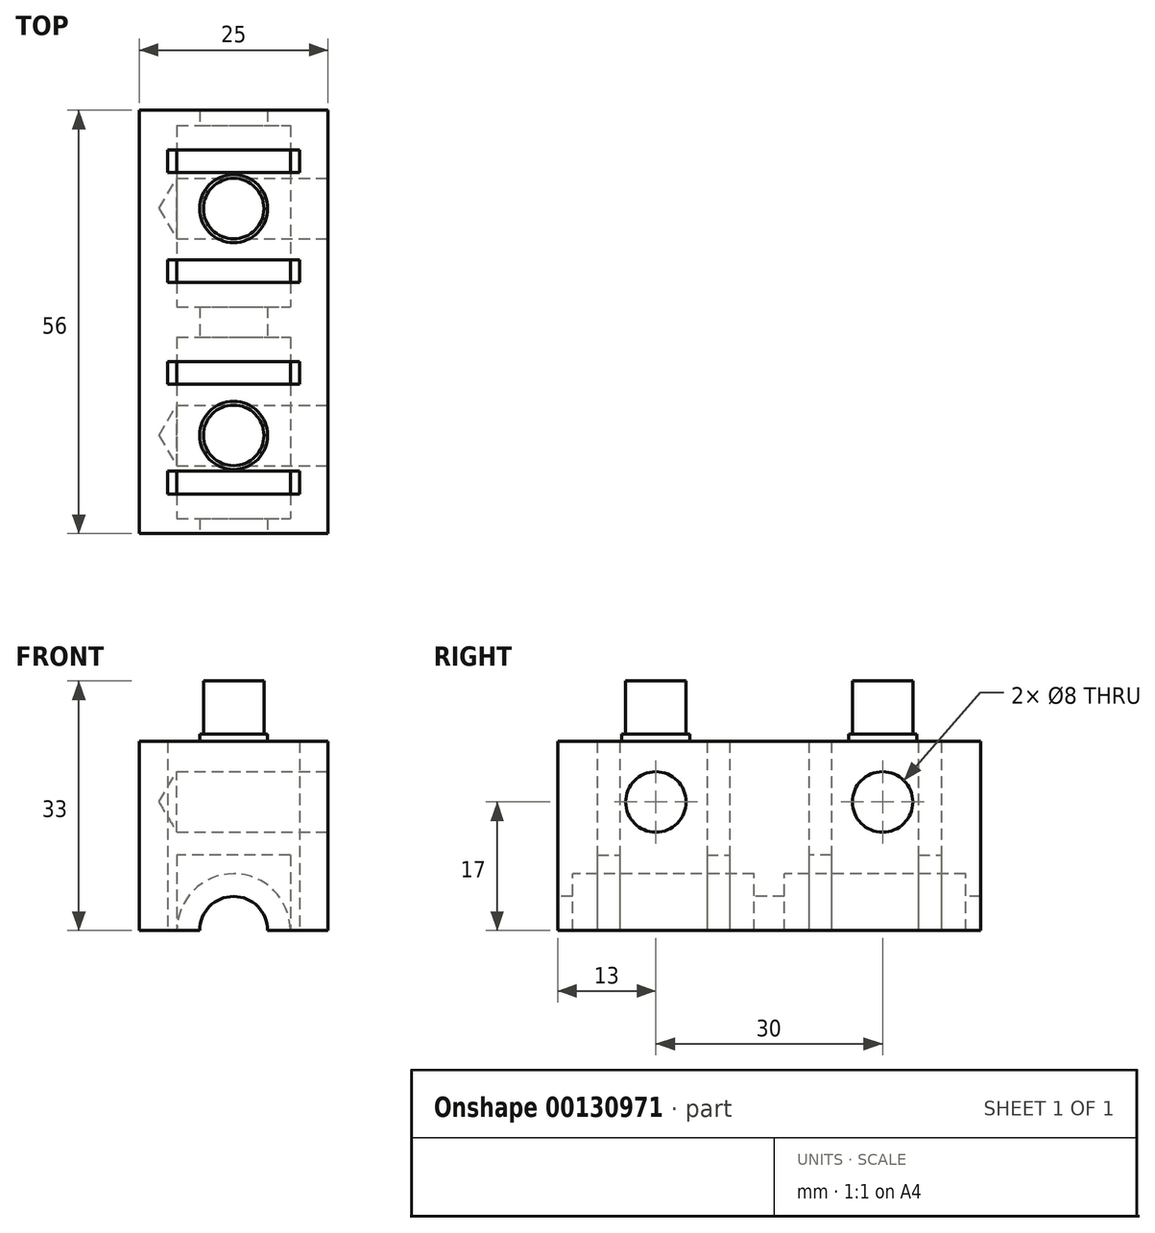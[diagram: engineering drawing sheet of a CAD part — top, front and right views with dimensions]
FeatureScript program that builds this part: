
annotation { "Feature Type Name" : "Feature", "Feature Type Description" : "" }
export const myFeature = defineFeature(function(context is Context, id is Id, definition is map)
    precondition{}
    {
        {
            var Q0;
            Q0=qCreatedBy(makeId("Top.planeOp"),FACE);
            var sketch = newSketch(context, id + "F0", { "sketchPlane" : qUnion([Q0])});
            skLineSegment(sketch, "E0.bottom", {"start": v(0, 0) * mm, "end": v(25, 0) * mm});
            skLineSegment(sketch, "E0.top", {"start": v(0, 56) * mm, "end": v(25, 56) * mm});
            skLineSegment(sketch, "E0.left", {"start": v(0, 0) * mm, "end": v(0, 56) * mm});
            skLineSegment(sketch, "E0.right", {"start": v(25, 0) * mm, "end": v(25, 56) * mm});
            skSolve(sketch);
        }
        {
            var Q0;
            Q0 = qSketchRegion(id + "F0", true);
            extrude(context, id + "F1", {"entities" : qUnion([Q0]), "depth" : 25 * mm});
        }
        {
            var Q0;
            Q0=makeQuery(id+"F1.opExtrude","SWEPT_FACE",FACE,{"disambiguationData":[OSD([sQuery(id+"F0.wireOp",EDGE,"E0.right")])]});
            var sketch = newSketch(context, id + "F2", { "sketchPlane" : qUnion([Q0])});
            skLineSegment(sketch, "E1", {"start": v(0, 17) * mm, "end": v(56, 17) * mm});
            skPoint(sketch, "E2", {"position": v(13, 17) * mm});
            skPoint(sketch, "E3", {"position": v(43, 17) * mm});
            skLineSegment(sketch, "E4", {"start": v(28, 25) * mm, "end": v(28, 0) * mm});
            skSolve(sketch);
        }
        {
            var Q0;
            Q0=makeQuery(id+"F1.opExtrude","SWEPT_FACE",FACE,{"disambiguationData":[OSD([sQuery(id+"F0.wireOp",EDGE,"E0.bottom")])]});
            var sketch = newSketch(context, id + "F3", { "sketchPlane" : qUnion([Q0])});
            skPoint(sketch, "E5", {"position": v(12.5, 0) * mm});
            skSolve(sketch);
        }
        {
            var Q0;
            Q0=sQuery(id+"F3.wireOp",VERTEX,"E5");
            var Q1;
            Q1=makeQuery(id+"F1.opExtrude","SWEPT_BODY",BODY,{"disambiguationData":[OSD([sQuery(id+"F0.wireOp",EDGE,"E0.bottom"),sQuery(id+"F0.wireOp",EDGE,"E0.top"),sQuery(id+"F0.wireOp",EDGE,"E0.left"),sQuery(id+"F0.wireOp",EDGE,"E0.right")])]});
            hole(context, id + "F4", {"style" : HoleStyle.SIMPLE, "endStyle" : HoleEndStyle.THROUGH, "holeDiameter" : 15 * mm, "locations" : qUnion([Q0]), "scope" : qUnion([Q1]), "isTappedThrough" : true});
        }
        {
            var Q0;
            Q0=sQuery(id+"F2.wireOp",VERTEX,"E2");
            var Q1;
            Q1=sQuery(id+"F2.wireOp",VERTEX,"E3");
            var Q2;
            Q2=makeQuery(id+"F1.opExtrude","SWEPT_BODY",BODY,{"disambiguationData":[OSD([sQuery(id+"F0.wireOp",EDGE,"E0.bottom"),sQuery(id+"F0.wireOp",EDGE,"E0.top"),sQuery(id+"F0.wireOp",EDGE,"E0.left"),sQuery(id+"F0.wireOp",EDGE,"E0.right")])]});
            hole(context, id + "F5", {"style" : HoleStyle.SIMPLE, "endStyle" : HoleEndStyle.BLIND, "holeDiameter" : 8 * mm, "holeDepth" : 20 * mm, "locations" : qUnion([Q0, Q1]), "scope" : qUnion([Q2])});
        }
        {
            var Q0;
            Q0=makeQuery(id+"F1.opExtrude","CAP_FACE",FACE,{"disambiguationData":[OSD([sQuery(id+"F0.wireOp",EDGE,"E0.bottom"),sQuery(id+"F0.wireOp",EDGE,"E0.top"),sQuery(id+"F0.wireOp",EDGE,"E0.left"),sQuery(id+"F0.wireOp",EDGE,"E0.right")])],"isStart":false});
            var sketch = newSketch(context, id + "F6", { "sketchPlane" : qUnion([Q0])});
            skLineSegment(sketch, "E6", {"start": v(12.5, 0) * mm, "end": v(12.5, 56) * mm});
            skLineSegment(sketch, "E7", {"start": v(0, 28) * mm, "end": v(25, 28) * mm});
            skPoint(sketch, "E8", {"position": v(12.5, 13) * mm});
            skPoint(sketch, "E9", {"position": v(12.5, 43) * mm});
            skCircle(sketch, "E10", {"center": v(12.5, 13) * mm, "radius": 4.5 * mm});
            skCircle(sketch, "E11", {"center": v(12.5, 43) * mm, "radius": 4.5 * mm});
            skSolve(sketch);
        }
        {
            var Q0;
            Q0 = qSketchRegion(id + "F6", true);
            extrude(context, id + "F7", {"entities" : qUnion([Q0]), "operationType" : NewBodyOperationType.ADD, "depth" : 1 * mm});
        }
        {
            var Q0;
            {var subQ0=sQuery(id+"F0.wireOp",EDGE,"E0.bottom");var subQ1=sQuery(id+"F0.wireOp",EDGE,"E0.top");var subQ2=sQuery(id+"F0.wireOp",EDGE,"E0.left");Q0=makeQuery(id+"F4.hole-0.boolean.opBoolean","SPLIT",FACE,{"disambiguationData":[TD([makeQuery(id+"F1.opExtrude","SWEPT_FACE",FACE,{"disambiguationData":[OSD([subQ2])]})])],"derivedFrom":makeQuery(id+"F1.opExtrude","CAP_FACE",FACE,{"disambiguationData":[OSD([subQ0,subQ1,subQ2,sQuery(id+"F0.wireOp",EDGE,"E0.right")])],"isStart":true})});}
            var sketch = newSketch(context, id + "F8", { "sketchPlane" : qUnion([Q0])});
            skLineSegment(sketch, "E12.bottom", {"start": v(0, 0) * mm, "end": v(25, 0) * mm});
            skLineSegment(sketch, "E12.top", {"start": v(0, -2) * mm, "end": v(25, -2) * mm});
            skLineSegment(sketch, "E12.left", {"start": v(0, 0) * mm, "end": v(0, -2) * mm});
            skLineSegment(sketch, "E12.right", {"start": v(25, 0) * mm, "end": v(25, -2) * mm});
            skLineSegment(sketch, "E13.bottom", {"start": v(0, -26) * mm, "end": v(25, -26) * mm});
            skLineSegment(sketch, "E13.top", {"start": v(0, -30) * mm, "end": v(25, -30) * mm});
            skLineSegment(sketch, "E13.left", {"start": v(0, -26) * mm, "end": v(0, -30) * mm});
            skLineSegment(sketch, "E13.right", {"start": v(25, -26) * mm, "end": v(25, -30) * mm});
            skLineSegment(sketch, "E14.bottom", {"start": v(0, -56) * mm, "end": v(25, -56) * mm});
            skLineSegment(sketch, "E14.top", {"start": v(0, -54) * mm, "end": v(25, -54) * mm});
            skLineSegment(sketch, "E14.left", {"start": v(0, -56) * mm, "end": v(0, -54) * mm});
            skLineSegment(sketch, "E14.right", {"start": v(25, -56) * mm, "end": v(25, -54) * mm});
            skLineSegment(sketch, "E15", {"start": v(0, -28) * mm, "end": v(45.7, -28) * mm});
            skSolve(sketch);
        }
        {
            var Q0;
            Q0 = qSketchRegion(id + "F8", true);
            extrude(context, id + "F9", {"entities" : qUnion([Q0]), "operationType" : NewBodyOperationType.ADD, "oppositeDirection" : true, "depth" : 8 * mm});
        }
        {
            var Q0;
            {var subQ0=sQuery(id+"F0.wireOp",EDGE,"E0.bottom");var subQ2=sQuery(id+"F0.wireOp",EDGE,"E0.top");var subQ4=sQuery(id+"F0.wireOp",EDGE,"E0.right");var subQ6=sQuery(id+"F0.wireOp",EDGE,"E0.left");var subQ7=makeQuery(id+"F1.opExtrude","CAP_FACE",FACE,{"disambiguationData":[OSD([subQ0,subQ2,subQ6,subQ4])],"isStart":true});Q0=makeQuery(id+"F9.boolean.opBoolean","MERGE",FACE,{"derivedFrom":[makeQuery(id+"F4.hole-0.boolean.opBoolean","SPLIT",FACE,{"disambiguationData":[TD([makeQuery(id+"F1.opExtrude","SWEPT_FACE",FACE,{"disambiguationData":[OSD([subQ6])]})])],"derivedFrom":subQ7}),makeQuery(id+"F4.hole-0.boolean.opBoolean","SPLIT",FACE,{"disambiguationData":[TD([makeQuery(id+"F1.opExtrude","SWEPT_FACE",FACE,{"disambiguationData":[OSD([subQ4])]})])],"derivedFrom":subQ7}),makeQuery(id+"F9.opExtrude","CAP_FACE",FACE,{"disambiguationData":[OSD([sQuery(id+"F8.wireOp",EDGE,"E12.bottom"),sQuery(id+"F8.wireOp",EDGE,"E12.top"),sQuery(id+"F8.wireOp",EDGE,"E12.left"),sQuery(id+"F8.wireOp",EDGE,"E12.right")])],"isStart":true}),makeQuery(id+"F9.opExtrude","CAP_FACE",FACE,{"disambiguationData":[OSD([sQuery(id+"F8.wireOp",EDGE,"E13.bottom"),sQuery(id+"F8.wireOp",EDGE,"E13.top"),sQuery(id+"F8.wireOp",EDGE,"E13.left"),sQuery(id+"F8.wireOp",EDGE,"E13.right")])],"isStart":true}),makeQuery(id+"F9.opExtrude","CAP_FACE",FACE,{"disambiguationData":[OSD([sQuery(id+"F8.wireOp",EDGE,"E14.bottom"),sQuery(id+"F8.wireOp",EDGE,"E14.top"),sQuery(id+"F8.wireOp",EDGE,"E14.left"),sQuery(id+"F8.wireOp",EDGE,"E14.right")])],"isStart":true})]});}
            var sketch = newSketch(context, id + "F10", { "sketchPlane" : qUnion([Q0])});
            skLineSegment(sketch, "E16", {"start": v(12.5, -2) * mm, "end": v(12.5, -54) * mm});
            skLineSegment(sketch, "E17", {"start": v(5, -42) * mm, "end": v(20, -42) * mm});
            skLineSegment(sketch, "E18", {"start": v(5, -14) * mm, "end": v(20, -14) * mm});
            skLineSegment(sketch, "E19.bottom", {"start": v(5, -5.25) * mm, "end": v(3.75, -5.25) * mm});
            skLineSegment(sketch, "E19.top", {"start": v(5, -8.25) * mm, "end": v(3.75, -8.25) * mm});
            skLineSegment(sketch, "E19.left", {"start": v(5, -5.25) * mm, "end": v(5, -8.25) * mm});
            skLineSegment(sketch, "E19.right", {"start": v(3.75, -5.25) * mm, "end": v(3.75, -8.25) * mm});
            skLineSegment(sketch, "E20.bottom", {"start": v(20, -5.25) * mm, "end": v(21.25, -5.25) * mm});
            skLineSegment(sketch, "E20.top", {"start": v(20, -8.25) * mm, "end": v(21.25, -8.25) * mm});
            skLineSegment(sketch, "E20.left", {"start": v(20, -5.25) * mm, "end": v(20, -8.25) * mm});
            skLineSegment(sketch, "E20.right", {"start": v(21.25, -5.25) * mm, "end": v(21.25, -8.25) * mm});
            skLineSegment(sketch, "E21.bottom", {"start": v(5, -22.75) * mm, "end": v(3.75, -22.75) * mm});
            skLineSegment(sketch, "E21.top", {"start": v(5, -19.75) * mm, "end": v(3.75, -19.75) * mm});
            skLineSegment(sketch, "E21.left", {"start": v(5, -22.75) * mm, "end": v(5, -19.75) * mm});
            skLineSegment(sketch, "E21.right", {"start": v(3.75, -22.75) * mm, "end": v(3.75, -19.75) * mm});
            skLineSegment(sketch, "E22.bottom", {"start": v(20, -22.75) * mm, "end": v(21.25, -22.75) * mm});
            skLineSegment(sketch, "E22.top", {"start": v(20, -19.75) * mm, "end": v(21.25, -19.75) * mm});
            skLineSegment(sketch, "E22.left", {"start": v(20, -22.75) * mm, "end": v(20, -19.75) * mm});
            skLineSegment(sketch, "E22.right", {"start": v(21.25, -22.75) * mm, "end": v(21.25, -19.75) * mm});
            skLineSegment(sketch, "E23", {"start": v(0, -28) * mm, "end": v(25, -28) * mm});
            skLineSegment(sketch, "E24.bottom", {"start": v(20, -47.75) * mm, "end": v(21.25, -47.75) * mm});
            skLineSegment(sketch, "E24.top", {"start": v(20, -50.75) * mm, "end": v(21.25, -50.75) * mm});
            skLineSegment(sketch, "E24.left", {"start": v(20, -47.75) * mm, "end": v(20, -50.75) * mm});
            skLineSegment(sketch, "E24.right", {"start": v(21.25, -47.75) * mm, "end": v(21.25, -50.75) * mm});
            skLineSegment(sketch, "E25.bottom", {"start": v(5, -47.75) * mm, "end": v(3.75, -47.75) * mm});
            skLineSegment(sketch, "E25.top", {"start": v(5, -50.75) * mm, "end": v(3.75, -50.75) * mm});
            skLineSegment(sketch, "E25.left", {"start": v(5, -47.75) * mm, "end": v(5, -50.75) * mm});
            skLineSegment(sketch, "E25.right", {"start": v(3.75, -47.75) * mm, "end": v(3.75, -50.75) * mm});
            skLineSegment(sketch, "E26.bottom", {"start": v(20, -33.25) * mm, "end": v(21.25, -33.25) * mm});
            skLineSegment(sketch, "E26.top", {"start": v(20, -36.25) * mm, "end": v(21.25, -36.25) * mm});
            skLineSegment(sketch, "E26.left", {"start": v(20, -33.25) * mm, "end": v(20, -36.25) * mm});
            skLineSegment(sketch, "E26.right", {"start": v(21.25, -33.25) * mm, "end": v(21.25, -36.25) * mm});
            skLineSegment(sketch, "E27.bottom", {"start": v(5, -33.25) * mm, "end": v(3.75, -33.25) * mm});
            skLineSegment(sketch, "E27.top", {"start": v(5, -36.25) * mm, "end": v(3.75, -36.25) * mm});
            skLineSegment(sketch, "E27.left", {"start": v(5, -33.25) * mm, "end": v(5, -36.25) * mm});
            skLineSegment(sketch, "E27.right", {"start": v(3.75, -33.25) * mm, "end": v(3.75, -36.25) * mm});
            skSolve(sketch);
        }
        {
            var Q0;
            Q0 = qSketchRegion(id + "F10", true);
            extrude(context, id + "F11", {"entities" : qUnion([Q0]), "operationType" : NewBodyOperationType.REMOVE, "endBound" : BoundingType.THROUGH_ALL, "oppositeDirection" : true, "depth" : 25 * mm});
        }
        {
            var Q0;
            Q0=makeQuery(id+"F1.opExtrude","CAP_FACE",FACE,{"disambiguationData":[OSD([sQuery(id+"F0.wireOp",EDGE,"E0.bottom"),sQuery(id+"F0.wireOp",EDGE,"E0.top"),sQuery(id+"F0.wireOp",EDGE,"E0.left"),sQuery(id+"F0.wireOp",EDGE,"E0.right")])],"isStart":false});
            var sketch = newSketch(context, id + "F12", { "sketchPlane" : qUnion([Q0])});
            skLineSegment(sketch, "E28.bottom", {"start": v(3.75, 8.25) * mm, "end": v(21.25, 8.25) * mm});
            skLineSegment(sketch, "E28.top", {"start": v(3.75, 5.25) * mm, "end": v(21.25, 5.25) * mm});
            skLineSegment(sketch, "E28.left", {"start": v(3.75, 8.25) * mm, "end": v(3.75, 5.25) * mm});
            skLineSegment(sketch, "E28.right", {"start": v(21.25, 8.25) * mm, "end": v(21.25, 5.25) * mm});
            skLineSegment(sketch, "E29.bottom", {"start": v(3.75, 22.75) * mm, "end": v(21.25, 22.75) * mm});
            skLineSegment(sketch, "E29.top", {"start": v(3.75, 19.75) * mm, "end": v(21.25, 19.75) * mm});
            skLineSegment(sketch, "E29.left", {"start": v(3.75, 22.75) * mm, "end": v(3.75, 19.75) * mm});
            skLineSegment(sketch, "E29.right", {"start": v(21.25, 22.75) * mm, "end": v(21.25, 19.75) * mm});
            skLineSegment(sketch, "E30.bottom", {"start": v(3.75, 36.25) * mm, "end": v(21.25, 36.25) * mm});
            skLineSegment(sketch, "E30.top", {"start": v(3.75, 33.25) * mm, "end": v(21.25, 33.25) * mm});
            skLineSegment(sketch, "E30.left", {"start": v(3.75, 36.25) * mm, "end": v(3.75, 33.25) * mm});
            skLineSegment(sketch, "E30.right", {"start": v(21.25, 36.25) * mm, "end": v(21.25, 33.25) * mm});
            skLineSegment(sketch, "E31.bottom", {"start": v(3.75, 50.75) * mm, "end": v(21.25, 50.75) * mm});
            skLineSegment(sketch, "E31.top", {"start": v(3.75, 47.75) * mm, "end": v(21.25, 47.75) * mm});
            skLineSegment(sketch, "E31.left", {"start": v(3.75, 50.75) * mm, "end": v(3.75, 47.75) * mm});
            skLineSegment(sketch, "E31.right", {"start": v(21.25, 50.75) * mm, "end": v(21.25, 47.75) * mm});
            skSolve(sketch);
        }
        {
            var Q0;
            Q0 = qSketchRegion(id + "F12", true);
            extrude(context, id + "F13", {"entities" : qUnion([Q0]), "operationType" : NewBodyOperationType.REMOVE, "oppositeDirection" : true, "depth" : 15 * mm});
        }
        {
            var Q0;
            Q0=makeQuery(id+"F7.opExtrude","CAP_FACE",FACE,{"disambiguationData":[OSD([sQuery(id+"F6.wireOp",EDGE,"E11")])],"isStart":false});
            var sketch = newSketch(context, id + "F14", { "sketchPlane" : qUnion([Q0])});
            skCircle(sketch, "E32", {"center": v(12.5, 43) * mm, "radius": 4 * mm});
            skSolve(sketch);
        }
        {
            var Q0;
            Q0=makeQuery(id+"F7.opExtrude","CAP_FACE",FACE,{"disambiguationData":[OSD([sQuery(id+"F6.wireOp",EDGE,"E10")])],"isStart":false});
            var sketch = newSketch(context, id + "F15", { "sketchPlane" : qUnion([Q0])});
            skCircle(sketch, "E33", {"center": v(12.5, 13) * mm, "radius": 4 * mm});
            skSolve(sketch);
        }
        {
            var Q0;
            Q0 = qSketchRegion(id + "F14", true);
            var Q1;
            Q1 = qSketchRegion(id + "F15", true);
            extrude(context, id + "F16", {"entities" : qUnion([Q0, Q1]), "operationType" : NewBodyOperationType.ADD, "depth" : 7 * mm});
        }
        {
            var Q0;
            Q0=makeQuery(id+"F9.boolean.opBoolean","MERGE",FACE,{"derivedFrom":[makeQuery(id+"F1.opExtrude","SWEPT_FACE",FACE,{"disambiguationData":[OSD([sQuery(id+"F0.wireOp",EDGE,"E0.bottom")])]}),makeQuery(id+"F9.opExtrude","SWEPT_FACE",FACE,{"disambiguationData":[OSD([sQuery(id+"F8.wireOp",EDGE,"E12.bottom")])]})]});
            var sketch = newSketch(context, id + "F17", { "sketchPlane" : qUnion([Q0])});
            skPoint(sketch, "E34", {"position": v(12.5, 0) * mm});
            skSolve(sketch);
        }
        {
            var Q0;
            Q0=sQuery(id+"F17.wireOp",VERTEX,"E34");
            var Q1;
            Q1=makeQuery(id+"F1.opExtrude","SWEPT_BODY",BODY,{"disambiguationData":[OSD([sQuery(id+"F0.wireOp",EDGE,"E0.bottom"),sQuery(id+"F0.wireOp",EDGE,"E0.top"),sQuery(id+"F0.wireOp",EDGE,"E0.left"),sQuery(id+"F0.wireOp",EDGE,"E0.right")])]});
            hole(context, id + "F18", {"style" : HoleStyle.SIMPLE, "endStyle" : HoleEndStyle.THROUGH, "holeDiameter" : 9 * mm, "locations" : qUnion([Q0]), "scope" : qUnion([Q1]), "isTappedThrough" : true});
        }
    });
